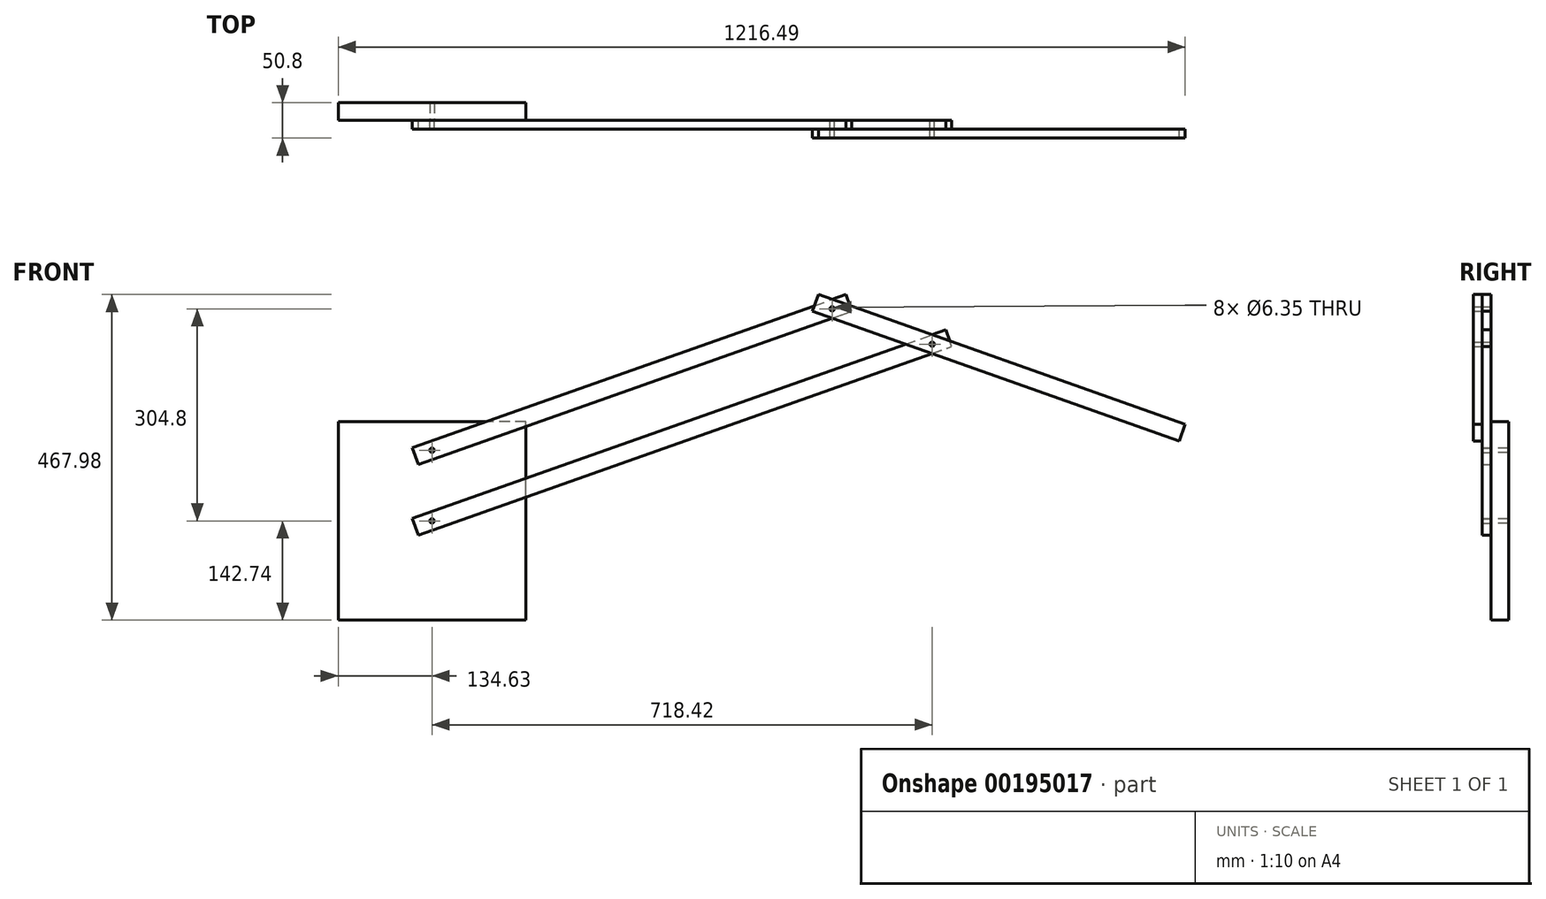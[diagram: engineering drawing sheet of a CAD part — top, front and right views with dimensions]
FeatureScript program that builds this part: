
annotation { "Feature Type Name" : "Feature", "Feature Type Description" : "" }
export const myFeature = defineFeature(function(context is Context, id is Id, definition is map)
    precondition{}
    {
        {
            var Q0;
            Q0=qCreatedBy(makeId("Front.planeOp"),FACE);
            var sketch = newSketch(context, id + "F0", { "sketchPlane" : qUnion([Q0])});
            skLineSegment(sketch, "E0", {"start": v(0, 101.6) * mm, "end": v(574.74, 304.8) * mm});
            skLineSegment(sketch, "E1", {"start": v(0, 0) * mm, "end": v(718.42, 254) * mm});
            skLineSegment(sketch, "E2", {"start": v(574.74, 304.8) * mm, "end": v(1053.68, 135.47) * mm});
            skSolve(sketch);
        }
        {
            var Q0;
            Q0=qCreatedBy(makeId("Front.planeOp"),FACE);
            var sketch = newSketch(context, id + "F1", { "sketchPlane" : qUnion([Q0])});
            skLineSegment(sketch, "E3.0", {"start": v(0, 101.6) * mm, "end": v(574.74, 304.8) * mm, "construction": true});
            skLineSegment(sketch, "E4.bottom", {"start": v(-19.71, 81.16) * mm, "end": v(602.92, 301.3) * mm});
            skLineSegment(sketch, "E4.top", {"start": v(-28.18, 105.1) * mm, "end": v(594.45, 325.24) * mm});
            skLineSegment(sketch, "E4.left", {"start": v(-19.71, 81.16) * mm, "end": v(-28.18, 105.1) * mm});
            skLineSegment(sketch, "E4.right", {"start": v(602.92, 301.3) * mm, "end": v(594.45, 325.24) * mm});
            skPoint(sketch, "E4.middle", {"position": v(287.37, 203.2) * mm});
            skLineSegment(sketch, "E5.0", {"start": v(0, 0) * mm, "end": v(718.42, 254) * mm, "construction": true});
            skLineSegment(sketch, "E6.bottom", {"start": v(-19.71, -20.44) * mm, "end": v(746.6, 250.5) * mm});
            skLineSegment(sketch, "E6.top", {"start": v(-28.18, 3.5) * mm, "end": v(738.13, 274.44) * mm});
            skLineSegment(sketch, "E6.left", {"start": v(-19.71, -20.44) * mm, "end": v(-28.18, 3.5) * mm});
            skLineSegment(sketch, "E6.right", {"start": v(746.6, 250.5) * mm, "end": v(738.13, 274.44) * mm});
            skPoint(sketch, "E6.middle", {"position": v(359.21, 127) * mm});
            skCircle(sketch, "E7", {"center": v(0, 101.6) * mm, "radius": 3.18 * mm});
            skCircle(sketch, "E8", {"center": v(0, 0) * mm, "radius": 3.18 * mm});
            skCircle(sketch, "E9", {"center": v(574.74, 304.8) * mm, "radius": 3.18 * mm});
            skCircle(sketch, "E10", {"center": v(718.42, 254) * mm, "radius": 3.18 * mm});
            skSolve(sketch);
        }
        {
            var Q0;
            Q0 = qSketchRegion(id + "F1", true);
            extrude(context, id + "F2", {"entities" : qUnion([Q0]), "depth" : 12.7 * mm});
        }
        {
            var Q0;
            Q0=makeQuery(id+"F2.opExtrude","CAP_FACE",FACE,{"disambiguationData":[OSD([sQuery(id+"F1.wireOp",EDGE,"E4.bottom"),sQuery(id+"F1.wireOp",EDGE,"E4.top"),sQuery(id+"F1.wireOp",EDGE,"E4.left"),sQuery(id+"F1.wireOp",EDGE,"E4.right"),sQuery(id+"F1.wireOp",EDGE,"E7"),sQuery(id+"F1.wireOp",EDGE,"E9")])],"isStart":false});
            var sketch = newSketch(context, id + "F3", { "sketchPlane" : qUnion([Q0])});
            skLineSegment(sketch, "E11.0", {"start": v(574.74, 304.8) * mm, "end": v(1053.68, 135.47) * mm, "construction": true});
            skLineSegment(sketch, "E12.bottom", {"start": v(555.02, 325.24) * mm, "end": v(1081.86, 138.97) * mm});
            skLineSegment(sketch, "E12.top", {"start": v(546.56, 301.3) * mm, "end": v(1073.4, 115.03) * mm});
            skLineSegment(sketch, "E12.left", {"start": v(555.02, 325.24) * mm, "end": v(546.56, 301.3) * mm});
            skLineSegment(sketch, "E12.right", {"start": v(1081.86, 138.97) * mm, "end": v(1073.4, 115.03) * mm});
            skPoint(sketch, "E12.middle", {"position": v(814.2, 220.13) * mm});
            skCircle(sketch, "E13.0", {"center": v(574.74, 304.8) * mm, "radius": 3.18 * mm});
            skCircle(sketch, "E14.0", {"center": v(718.42, 254) * mm, "radius": 3.18 * mm});
            skSolve(sketch);
        }
        {
            var Q0;
            Q0 = qSketchRegion(id + "F3", true);
            extrude(context, id + "F4", {"entities" : qUnion([Q0]), "depth" : 12.7 * mm});
        }
        {
            var Q0;
            Q0=qCreatedBy(makeId("Front.planeOp"),FACE);
            var sketch = newSketch(context, id + "F5", { "sketchPlane" : qUnion([Q0])});
            skLineSegment(sketch, "E15.bottom", {"start": v(134.63, -142.74) * mm, "end": v(-134.63, -142.74) * mm});
            skLineSegment(sketch, "E15.top", {"start": v(134.63, 142.74) * mm, "end": v(-134.63, 142.74) * mm});
            skLineSegment(sketch, "E15.left", {"start": v(134.63, -142.74) * mm, "end": v(134.63, 142.74) * mm});
            skLineSegment(sketch, "E15.right", {"start": v(-134.63, -142.74) * mm, "end": v(-134.63, 142.74) * mm});
            skPoint(sketch, "E15.middle", {"position": v(0, 0) * mm});
            skCircle(sketch, "E16.0", {"center": v(0, 101.6) * mm, "radius": 3.18 * mm});
            skCircle(sketch, "E17.0", {"center": v(0, 0) * mm, "radius": 3.18 * mm});
            skSolve(sketch);
        }
        {
            var Q0;
            Q0 = qSketchRegion(id + "F5", true);
            extrude(context, id + "F6", {"entities" : qUnion([Q0]), "oppositeDirection" : true, "depth" : 25.4 * mm});
        }
    });
